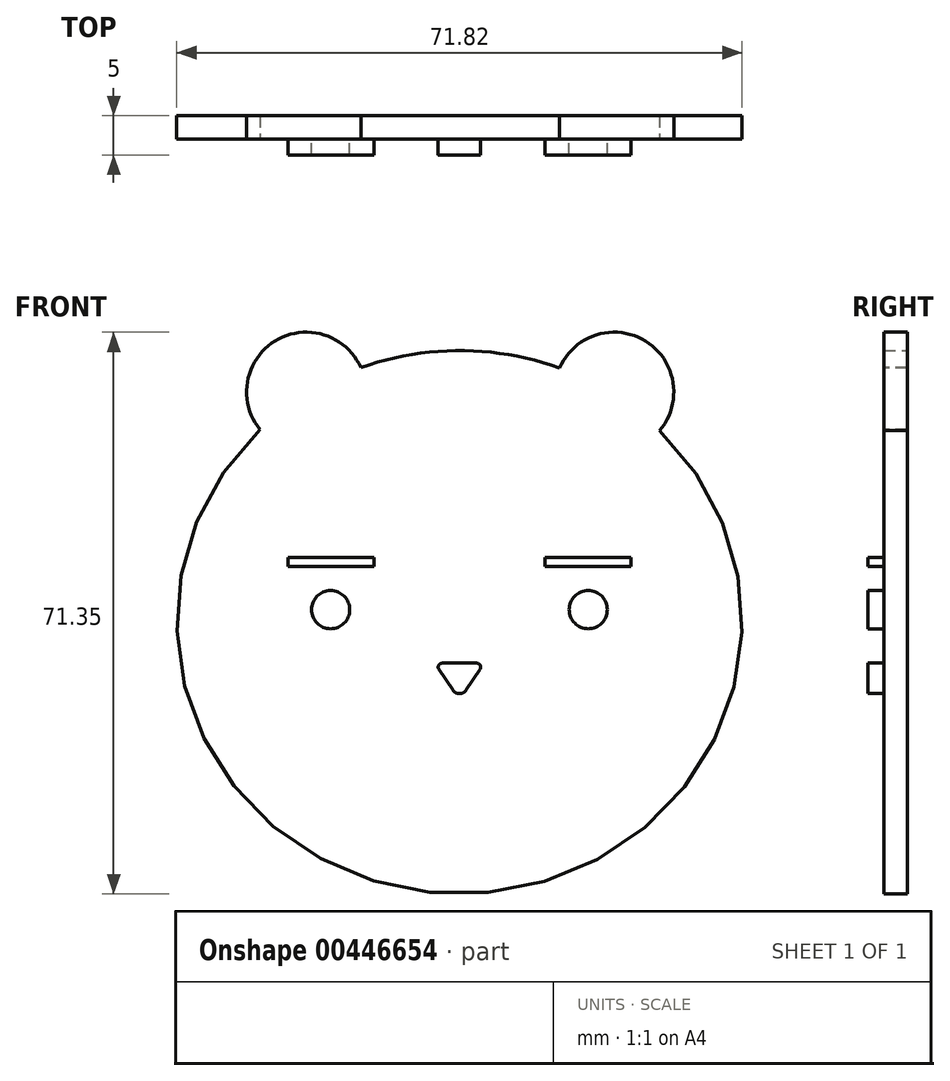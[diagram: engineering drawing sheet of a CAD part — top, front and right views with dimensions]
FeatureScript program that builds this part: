
annotation { "Feature Type Name" : "Feature", "Feature Type Description" : "" }
export const myFeature = defineFeature(function(context is Context, id is Id, definition is map)
    precondition{}
    {
        {
            var Q0;
            Q0=qCreatedBy(makeId("Front.planeOp"),FACE);
            var sketch = newSketch(context, id + "F0", { "sketchPlane" : qUnion([Q0])});
            skArc(sketch, "E0", {"start": v(-12.53, 32.34) * mm, "mid": v(-23.43, 35.72) * mm, "end": v(-25.32, 24.46) * mm});
            skArc(sketch, "E1", {"start": v(25.43, 24.36) * mm, "mid": v(23.65, 35.7) * mm, "end": v(12.7, 32.28) * mm});
            skEllipse(sketch, "E2", {"center": v(0, 0) * mm, "majorRadius": 34.5 * mm, "minorRadius": 35.9 * mm, "majorAxis": v(0, 1)});
            skSolve(sketch);
        }
        {
            var Q0;
            Q0=qCreatedBy(makeId("Front.planeOp"),FACE);
            var sketch = newSketch(context, id + "F1", { "sketchPlane" : qUnion([Q0])});
            skCircle(sketch, "E3", {"center": v(-16.36, 1.59) * mm, "radius": 2.42 * mm});
            skLineSegment(sketch, "E4", {"start": v(-21.8, 7.05) * mm, "end": v(-10.88, 7.05) * mm});
            skLineSegment(sketch, "E5", {"start": v(-10.88, 7.05) * mm, "end": v(-10.88, 8.25) * mm});
            skLineSegment(sketch, "E6", {"start": v(-10.88, 8.25) * mm, "end": v(-21.8, 8.25) * mm});
            skLineSegment(sketch, "E7", {"start": v(-21.8, 7.05) * mm, "end": v(-21.8, 8.25) * mm});
            skLineSegment(sketch, "E8.MirrorCS", {"start": v(10.88, 7.05) * mm, "end": v(10.88, 8.25) * mm});
            skLineSegment(sketch, "E9.MirrorCS", {"start": v(21.8, 7.05) * mm, "end": v(21.8, 8.25) * mm});
            skLineSegment(sketch, "E10.MirrorCS", {"start": v(21.8, 7.05) * mm, "end": v(10.88, 7.05) * mm});
            skLineSegment(sketch, "E11.MirrorCS", {"start": v(10.88, 8.25) * mm, "end": v(21.8, 8.25) * mm});
            skCircle(sketch, "E12.MirrorC", {"center": v(16.36, 1.59) * mm, "radius": 2.42 * mm});
            skLineSegment(sketch, "E13", {"start": v(0, -5.21) * mm, "end": v(-2.2, -5.21) * mm});
            skLineSegment(sketch, "E14", {"start": v(-2.62, -6) * mm, "end": v(-0.84, -8.64) * mm});
            skPoint(sketch, "E15.visualSharp", {"position": v(-3.15, -5.21) * mm});
            skArc(sketch, "E15.filletArc", {"start": v(-2.2, -5.21) * mm, "mid": v(-2.64, -5.48) * mm, "end": v(-2.62, -6) * mm});
            skArc(sketch, "E16.MirrorCS", {"start": v(2.2, -5.21) * mm, "mid": v(2.64, -5.48) * mm, "end": v(2.62, -6) * mm});
            skLineSegment(sketch, "E17.MirrorCS", {"start": v(2.62, -6) * mm, "end": v(0.84, -8.64) * mm});
            skLineSegment(sketch, "E18.MirrorCS", {"start": v(0, -5.21) * mm, "end": v(2.2, -5.21) * mm});
            skPoint(sketch, "E19.MirrorP", {"position": v(3.15, -5.21) * mm});
            skPoint(sketch, "E20.visualSharp", {"position": v(0, -9.89) * mm});
            skArc(sketch, "E20.filletArc", {"start": v(-0.84, -8.64) * mm, "mid": v(0, -9.08) * mm, "end": v(0.84, -8.64) * mm});
            skSolve(sketch);
        }
        {
            var Q0;
            Q0 = qSketchRegion(id + "F0", true);
            extrude(context, id + "F2", {"entities" : qUnion([Q0]), "oppositeDirection" : true, "depth" : 3 * mm});
        }
        {
            var Q0;
            Q0 = qSketchRegion(id + "F1", true);
            extrude(context, id + "F3", {"entities" : qUnion([Q0]), "operationType" : NewBodyOperationType.ADD, "depth" : 2 * mm});
        }
    });
